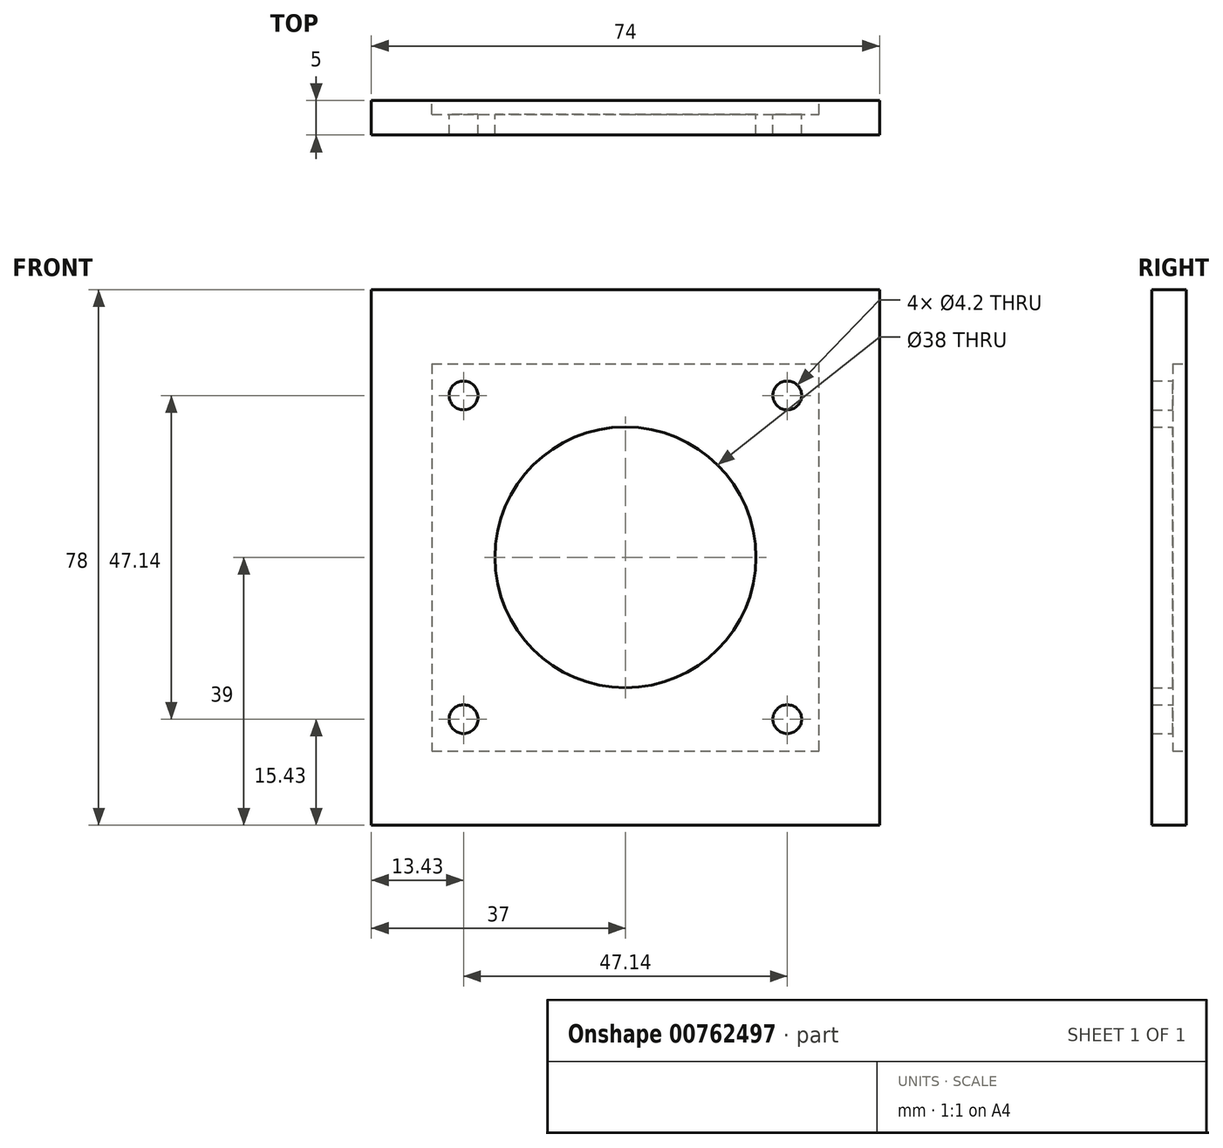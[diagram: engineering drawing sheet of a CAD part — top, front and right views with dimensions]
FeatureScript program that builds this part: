
annotation { "Feature Type Name" : "Feature", "Feature Type Description" : "" }
export const myFeature = defineFeature(function(context is Context, id is Id, definition is map)
    precondition{}
    {
        {
            var Q0;
            Q0=qCreatedBy(makeId("Front.planeOp"),FACE);
            var sketch = newSketch(context, id + "F0", { "sketchPlane" : qUnion([Q0])});
            skLineSegment(sketch, "E0.top", {"start": v(0, 39) * mm, "end": v(-74, 39) * mm});
            skLineSegment(sketch, "E0.left", {"start": v(0, 0) * mm, "end": v(0, 39) * mm});
            skLineSegment(sketch, "E0.right", {"start": v(-74, 0) * mm, "end": v(-74, 39) * mm});
            skLineSegment(sketch, "E1", {"start": v(-37, 19.5) * mm, "end": v(-37, 19) * mm});
            skArc(sketch, "E2", {"start": v(-18, 0) * mm, "mid": v(-37, 19) * mm, "end": v(-56, 0) * mm});
            skCircle(sketch, "E3", {"center": v(-60.57, 23.57) * mm, "radius": 2.1 * mm});
            skCircle(sketch, "E4", {"center": v(-13.43, 23.57) * mm, "radius": 2.1 * mm});
            skLineSegment(sketch, "E5", {"start": v(-74, 28.2) * mm, "end": v(0, 28.2) * mm});
            skLineSegment(sketch, "E6", {"start": v(-8.8, 39) * mm, "end": v(-8.8, 0) * mm});
            skLineSegment(sketch, "E7", {"start": v(-65.2, 39) * mm, "end": v(-65.2, 0) * mm});
            skLineSegment(sketch, "E8.MirrorCS", {"start": v(-37, -19.5) * mm, "end": v(-37, -19) * mm});
            skCircle(sketch, "E9.MirrorC", {"center": v(-13.43, -23.57) * mm, "radius": 2.1 * mm});
            skLineSegment(sketch, "E10.MirrorCS", {"start": v(0, 0) * mm, "end": v(0, -39) * mm});
            skCircle(sketch, "E11.MirrorC", {"center": v(-60.57, -23.57) * mm, "radius": 2.1 * mm});
            skLineSegment(sketch, "E12.MirrorCS", {"start": v(-65.2, -39) * mm, "end": v(-65.2, 0) * mm});
            skLineSegment(sketch, "E13.MirrorCS", {"start": v(-74, -28.2) * mm, "end": v(0, -28.2) * mm});
            skLineSegment(sketch, "E14.MirrorCS", {"start": v(-74, 0) * mm, "end": v(-74, -39) * mm});
            skLineSegment(sketch, "E15.MirrorCS", {"start": v(0, -39) * mm, "end": v(-74, -39) * mm});
            skArc(sketch, "E16.MirrorCS", {"start": v(-18, 0) * mm, "mid": v(-37, -19) * mm, "end": v(-56, 0) * mm});
            skLineSegment(sketch, "E17.MirrorCS", {"start": v(-8.8, -39) * mm, "end": v(-8.8, 0) * mm});
            skSolve(sketch);
        }
        {
            var Q0;
            Q0=qSketchRegion(id+"F0",true);
            var Q1;
            Q1=makeQuery(id+"F0.imprint","IMPRINT",FACE,{"disambiguationData":[TD([[makeQuery(id+"F0.imprint","IMPRINT",EDGE,{"derivedFrom":sQuery(id+"F0.wireOp",EDGE,"E3")}),-1.0]])]});
            extrude(context, id + "F1", {"entities" : qUnion([Q0, Q1]), "depth" : 5 * mm, "offsetDistance" : 25 * mm});
        }
        {
            var Q0;
            Q0=makeQuery(id+"F0.imprint","IMPRINT",FACE,{"disambiguationData":[TD([[makeQuery(id+"F0.imprint","IMPRINT",EDGE,{"derivedFrom":sQuery(id+"F0.wireOp",EDGE,"E3")}),-1.0]])]});
            extrude(context, id + "F2", {"entities" : qUnion([Q0]), "operationType" : NewBodyOperationType.REMOVE, "depth" : 2 * mm, "offsetDistance" : 25 * mm});
        }
    });
